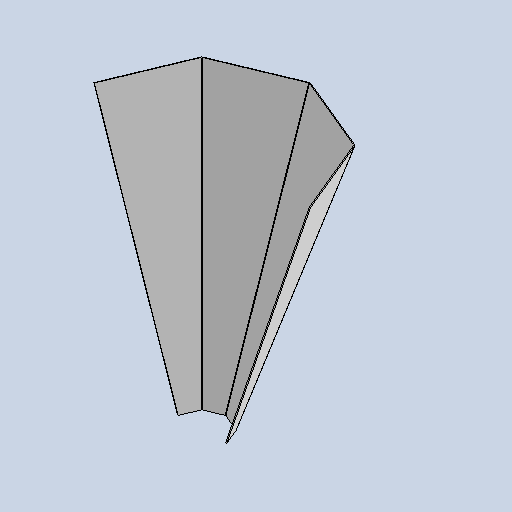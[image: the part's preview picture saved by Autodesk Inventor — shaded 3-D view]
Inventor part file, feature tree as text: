
AUTODESK INVENTOR PART (.ipt)
format: ipt  version: 2025.1 (Build 291241020, 241B)  size: 234,496 bytes
history: native  units: mm
features: sketch x2, plane x1, loft x1, sheet_metal_op x1, other x1
ambient origin geometry x8: Origin, YZ Plane, XZ Plane, XY Plane, X Axis, Y Axis, Z Axis, Center Point
bodies: Body1 (feature_tree)
feature tree (6):
  sketch  "Sketch15"  dims[d116=38.0mm d117=515.0mm]
  plane  "Work Plane1"
  loft  "Lofted Flange1"
  sketch  "Sketch16"  dims[d118=450.0mm d119=2.0mm d120=0.5mm d121=2.0mm d122=2.0mm d123=1.0mm d124=4.0mm d125=2.0mm]
  sheet_metal_op  "Bend1"
  other  "Definition1"
